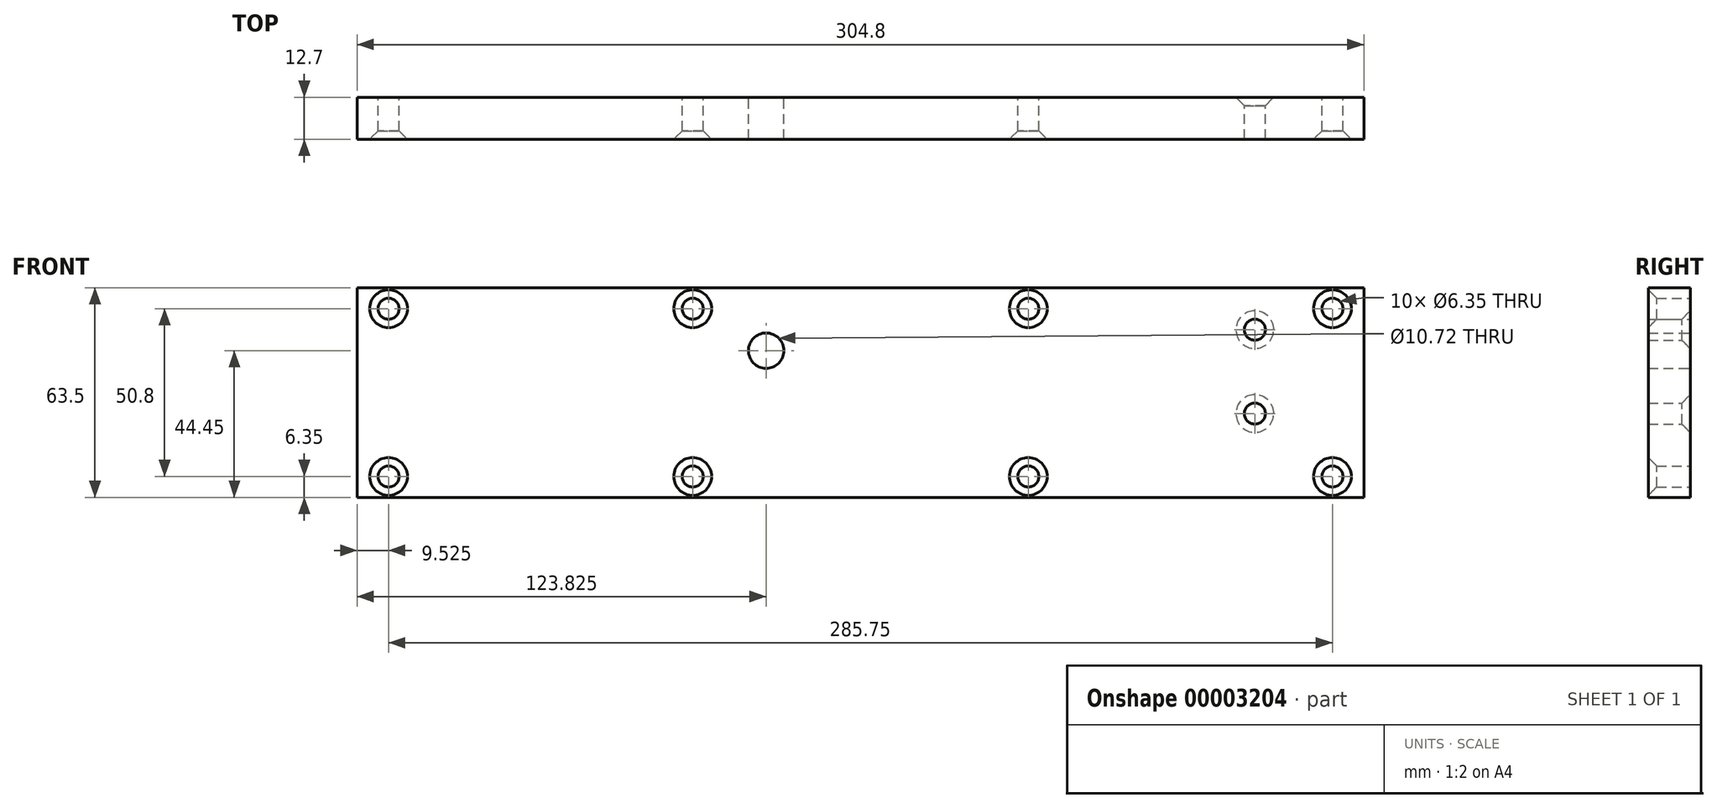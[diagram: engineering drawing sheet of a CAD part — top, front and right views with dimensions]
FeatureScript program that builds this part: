
annotation { "Feature Type Name" : "Feature", "Feature Type Description" : "" }
export const myFeature = defineFeature(function(context is Context, id is Id, definition is map)
    precondition{}
    {
        {
            var Q0;
            Q0=qCreatedBy(makeId("Front.planeOp"),FACE);
            var sketch = newSketch(context, id + "F0", { "sketchPlane" : qUnion([Q0])});
            skLineSegment(sketch, "E0", {"start": v(0, 0) * mm, "end": v(0, -63.5) * mm});
            skLineSegment(sketch, "E1", {"start": v(0, -63.5) * mm, "end": v(304.8, -63.5) * mm});
            skLineSegment(sketch, "E2", {"start": v(304.8, -63.5) * mm, "end": v(304.8, 0) * mm});
            skLineSegment(sketch, "E3", {"start": v(304.8, 0) * mm, "end": v(0, 0) * mm});
            skLineSegment(sketch, "E4", {"start": v(0, -6.35) * mm, "end": v(304.8, -6.35) * mm, "construction": true});
            skLineSegment(sketch, "E5", {"start": v(9.52, 0) * mm, "end": v(9.53, -63.5) * mm, "construction": true});
            skLineSegment(sketch, "E6", {"start": v(295.28, 0) * mm, "end": v(295.28, -63.5) * mm, "construction": true});
            skLineSegment(sketch, "E7", {"start": v(0, -57.15) * mm, "end": v(304.8, -57.15) * mm, "construction": true});
            skLineSegment(sketch, "E8", {"start": v(101.6, 0) * mm, "end": v(101.6, -63.5) * mm, "construction": true});
            skLineSegment(sketch, "E9", {"start": v(271.78, 0) * mm, "end": v(271.78, -63.5) * mm, "construction": true});
            skLineSegment(sketch, "E10", {"start": v(203.2, 0) * mm, "end": v(203.2, -63.5) * mm, "construction": true});
            skLineSegment(sketch, "E11", {"start": v(304.8, -12.7) * mm, "end": v(254, -12.7) * mm, "construction": true});
            skLineSegment(sketch, "E12", {"start": v(304.8, -38.1) * mm, "end": v(256.88, -38.1) * mm, "construction": true});
            skCircle(sketch, "E13", {"center": v(9.53, -6.35) * mm, "radius": 3.18 * mm});
            skCircle(sketch, "E14", {"center": v(9.53, -57.15) * mm, "radius": 3.18 * mm});
            skCircle(sketch, "E15", {"center": v(101.6, -57.15) * mm, "radius": 3.18 * mm});
            skCircle(sketch, "E16", {"center": v(101.6, -6.35) * mm, "radius": 3.18 * mm});
            skCircle(sketch, "E17", {"center": v(271.78, -12.7) * mm, "radius": 3.18 * mm});
            skCircle(sketch, "E18", {"center": v(271.78, -38.1) * mm, "radius": 3.18 * mm});
            skCircle(sketch, "E19", {"center": v(295.28, -57.15) * mm, "radius": 3.18 * mm});
            skCircle(sketch, "E20", {"center": v(295.28, -6.35) * mm, "radius": 3.18 * mm});
            skLineSegment(sketch, "E21", {"start": v(304.8, -19.05) * mm, "end": v(113.05, -19.05) * mm, "construction": true});
            skLineSegment(sketch, "E22", {"start": v(123.82, 0) * mm, "end": v(123.82, -63.5) * mm, "construction": true});
            skCircle(sketch, "E23", {"center": v(123.82, -19.05) * mm, "radius": 5.36 * mm});
            skCircle(sketch, "E24", {"center": v(203.2, -6.35) * mm, "radius": 3.18 * mm});
            skCircle(sketch, "E25", {"center": v(203.2, -57.15) * mm, "radius": 3.18 * mm});
            skSolve(sketch);
        }
        {
            var Q0;
            Q0=makeQuery(id+"F0.imprint","IMPRINT",FACE,{"disambiguationData":[TD([[makeQuery(id+"F0.imprint","IMPRINT",EDGE,{"derivedFrom":sQuery(id+"F0.wireOp",EDGE,"E0")}),1.0]])]});
            extrude(context, id + "F1", {"entities" : qUnion([Q0]), "endBound" : BoundingType.SYMMETRIC, "depth" : 12.7 * mm});
        }
        {
            var Q0;
            Q0=makeQuery(id+"F1.opExtrude","CAP_EDGE",EDGE,{"disambiguationData":[OSD([sQuery(id+"F0.wireOp",EDGE,"E13")])],"isStart":false});
            var Q1;
            Q1=makeQuery(id+"F1.opExtrude","CAP_EDGE",EDGE,{"disambiguationData":[OSD([sQuery(id+"F0.wireOp",EDGE,"E14")])],"isStart":false});
            var Q2;
            Q2=makeQuery(id+"F1.opExtrude","CAP_EDGE",EDGE,{"disambiguationData":[OSD([sQuery(id+"F0.wireOp",EDGE,"E16")])],"isStart":false});
            var Q3;
            Q3=makeQuery(id+"F1.opExtrude","CAP_EDGE",EDGE,{"disambiguationData":[OSD([sQuery(id+"F0.wireOp",EDGE,"E15")])],"isStart":false});
            var Q4;
            Q4=makeQuery(id+"F1.opExtrude","CAP_EDGE",EDGE,{"disambiguationData":[OSD([sQuery(id+"F0.wireOp",EDGE,"E20")])],"isStart":false});
            var Q5;
            Q5=makeQuery(id+"F1.opExtrude","CAP_EDGE",EDGE,{"disambiguationData":[OSD([sQuery(id+"F0.wireOp",EDGE,"E19")])],"isStart":false});
            var Q6;
            Q6=makeQuery(id+"F1.opExtrude","CAP_EDGE",EDGE,{"disambiguationData":[OSD([sQuery(id+"F0.wireOp",EDGE,"E17")])],"isStart":true});
            var Q7;
            Q7=makeQuery(id+"F1.opExtrude","CAP_EDGE",EDGE,{"disambiguationData":[OSD([sQuery(id+"F0.wireOp",EDGE,"E18")])],"isStart":true});
            var Q8;
            Q8=makeQuery(id+"F1.opExtrude","CAP_EDGE",EDGE,{"disambiguationData":[OSD([sQuery(id+"F0.wireOp",EDGE,"E24")])],"isStart":false});
            var Q9;
            Q9=makeQuery(id+"F1.opExtrude","CAP_EDGE",EDGE,{"disambiguationData":[OSD([sQuery(id+"F0.wireOp",EDGE,"E25")])],"isStart":false});
            chamfer(context, id + "F2", {"entities" : qUnion([Q0, Q1, Q2, Q3, Q4, Q5, Q6, Q7, Q8, Q9]), "chamferType" : ChamferType.OFFSET_ANGLE, "width" : 2.54 * mm, "oppositeDirection" : false, "angle" : 45 * degree, "tangentPropagation" : true});
        }
    });
